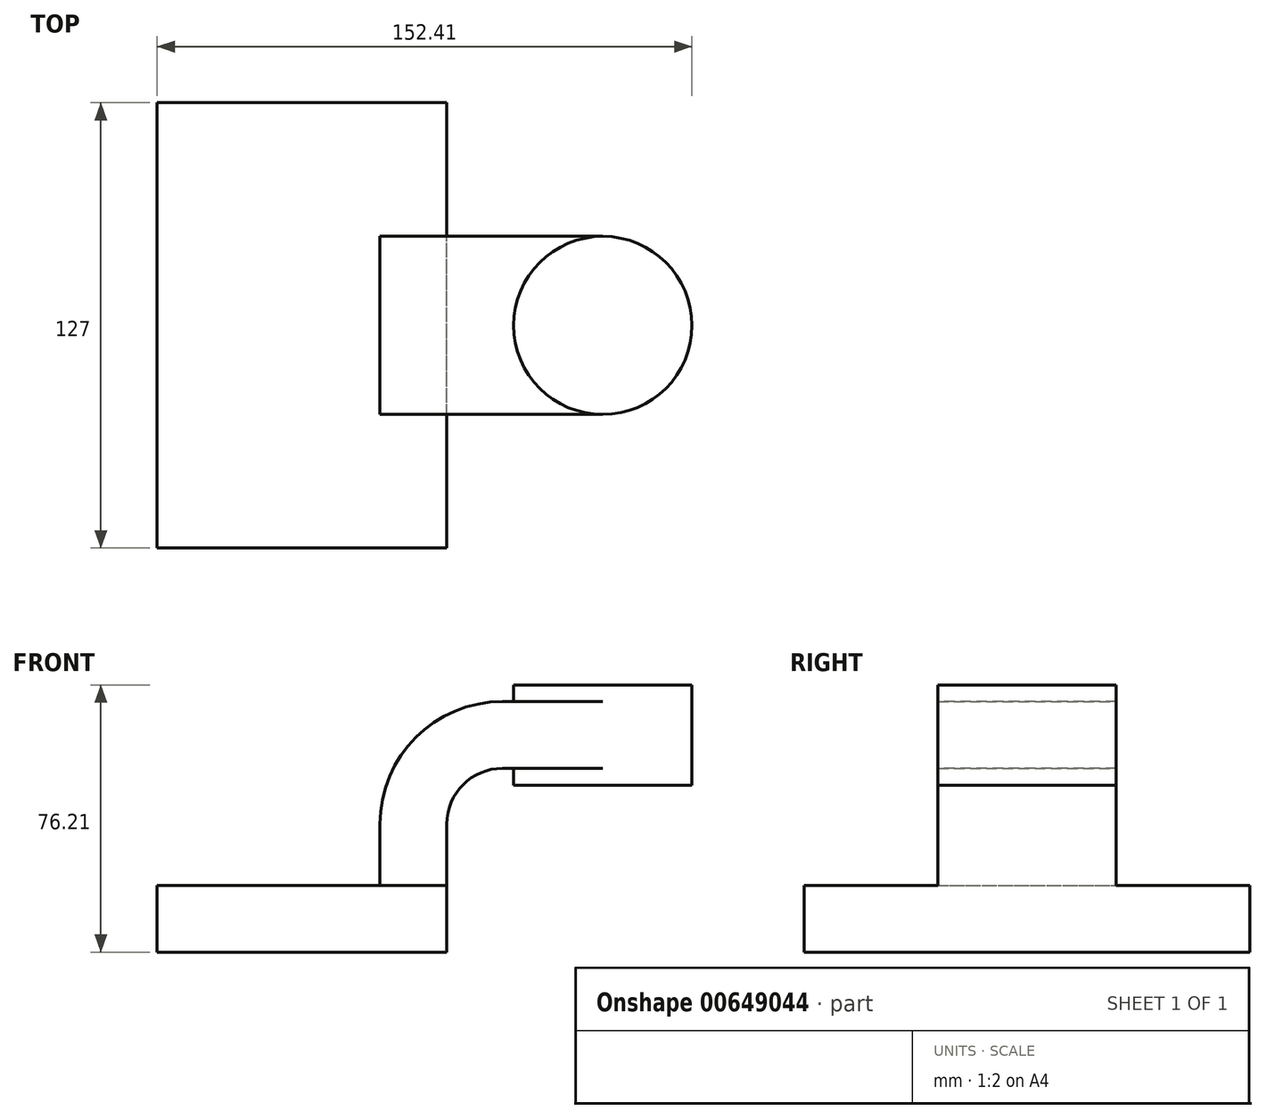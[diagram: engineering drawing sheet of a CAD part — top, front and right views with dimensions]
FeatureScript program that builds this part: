
annotation { "Feature Type Name" : "Feature", "Feature Type Description" : "" }
export const myFeature = defineFeature(function(context is Context, id is Id, definition is map)
    precondition{}
    {
        {
            var Q0;
            Q0=qCreatedBy(makeId("Front.planeOp"),FACE);
            var sketch = newSketch(context, id + "F0", { "sketchPlane" : qUnion([Q0])});
            skLineSegment(sketch, "E0.bottom", {"start": v(-41.28, -9.53) * mm, "end": v(41.28, -9.53) * mm});
            skLineSegment(sketch, "E0.top", {"start": v(-41.28, 9.53) * mm, "end": v(41.28, 9.53) * mm});
            skLineSegment(sketch, "E0.left", {"start": v(-41.28, -9.53) * mm, "end": v(-41.28, 9.53) * mm});
            skLineSegment(sketch, "E0.right", {"start": v(41.28, -9.53) * mm, "end": v(41.28, 9.53) * mm});
            skPoint(sketch, "E0.middle", {"position": v(0, 0) * mm});
            skLineSegment(sketch, "E1.bottom", {"start": v(60.32, 66.68) * mm, "end": v(111.12, 66.68) * mm});
            skLineSegment(sketch, "E1.top", {"start": v(60.32, 38.1) * mm, "end": v(111.12, 38.1) * mm});
            skLineSegment(sketch, "E1.left", {"start": v(60.32, 66.67) * mm, "end": v(60.32, 38.1) * mm});
            skLineSegment(sketch, "E1.right", {"start": v(111.12, 66.67) * mm, "end": v(111.12, 38.1) * mm});
            skPoint(sketch, "E1.middle", {"position": v(85.72, 52.39) * mm});
            skLineSegment(sketch, "E2", {"start": v(41.28, 9.52) * mm, "end": v(41.28, 27) * mm});
            skArc(sketch, "E3", {"start": v(41.27, 27) * mm, "mid": v(45.92, 38.23) * mm, "end": v(57.15, 42.88) * mm});
            skLineSegment(sketch, "E4", {"start": v(57.15, 42.88) * mm, "end": v(85.72, 42.88) * mm});
            skLineSegment(sketch, "E5.0", {"start": v(57.15, 61.93) * mm, "end": v(85.72, 61.93) * mm});
            skArc(sketch, "E5.1", {"start": v(22.22, 27) * mm, "mid": v(32.45, 51.7) * mm, "end": v(57.15, 61.93) * mm});
            skLineSegment(sketch, "E5.2", {"start": v(22.22, 9.52) * mm, "end": v(22.22, 27) * mm});
            skLineSegment(sketch, "E6", {"start": v(85.72, 66.68) * mm, "end": v(85.72, 38.1) * mm});
            skFitSpline(sketch, "E7", {"points": [v(-41.28, 9.53) * mm, v(57.15, 61.93) * mm], "startDerivative": vector(-28.63, 106.5) * mm, "endDerivative": vector(162.66, -29.62) * mm});
            skSolve(sketch);
        }
        {
            var Q0;
            Q0=makeQuery(id+"F0.imprint","IMPRINT",FACE,{"disambiguationData":[TD([[makeQuery(id+"F0.imprint","IMPRINT",EDGE,{"derivedFrom":sQuery(id+"F0.wireOp",EDGE,"E0.bottom")}),1.0]])]});
            extrude(context, id + "F1", {"entities" : qUnion([Q0]), "endBound" : BoundingType.SYMMETRIC, "depth" : 127 * mm, "offsetDistance" : 25.4 * mm});
        }
        {
            var Q0;
            {var subQ1=sQuery(id+"F0.wireOp",EDGE,"E2");Q0=makeQuery(id+"F0.imprint","IMPRINT",FACE,{"disambiguationData":[TD([[makeQuery(id+"F0.imprint","IMPRINT",EDGE,{"derivedFrom":subQ1}),1.0]])]});}
            var Q1;
            {var subQ0=sQuery(id+"F0.wireOp",EDGE,"E5.0");var subQ1=sQuery(id+"F0.wireOp",EDGE,"E1.left");var subQ2=makeQuery(id+"F0.imprint","INTERSECT",VERTEX,{"derivedFrom":[subQ1,subQ0]});Q1=makeQuery(id+"F0.imprint","IMPRINT",FACE,{"disambiguationData":[TD([[makeQuery(id+"F0.imprint","IMPRINT",EDGE,{"disambiguationData":[TD([[subQ2,-1.0]])],"derivedFrom":subQ1}),1.0]])]});}
            extrude(context, id + "F2", {"entities" : qUnion([Q0, Q1]), "operationType" : NewBodyOperationType.ADD, "endBound" : BoundingType.SYMMETRIC, "depth" : 50.8 * mm, "offsetDistance" : 25.4 * mm});
        }
        {
            var Q0;
            Q0=makeQuery(id+"F0.imprint","IMPRINT",FACE,{"disambiguationData":[TD([[makeQuery(id+"F0.imprint","IMPRINT",EDGE,{"derivedFrom":sQuery(id+"F0.wireOp",EDGE,"E5.1")}),1.0]])]});
            extrude(context, id + "F3", {"entities" : qUnion([Q0]), "operationType" : NewBodyOperationType.ADD, "endBound" : BoundingType.SYMMETRIC, "depth" : 16.5 * mm, "offsetDistance" : 25.4 * mm});
        }
        {
            var Q0;
            {var subQ0=sQuery(id+"F0.wireOp",EDGE,"E1.right");Q0=makeQuery(id+"F0.imprint","IMPRINT",FACE,{"disambiguationData":[TD([[makeQuery(id+"F0.imprint","IMPRINT",EDGE,{"derivedFrom":subQ0}),-1.0]])]});}
            var Q1;
            Q1=sQuery(id+"F0.wireOp",EDGE,"E6");
            revolve(context, id + "F4", {"operationType" : NewBodyOperationType.ADD, "entities" : qUnion([Q0]), "axis" : qUnion([Q1]), "revolveType" : RevolveType.FULL});
        }
    });
